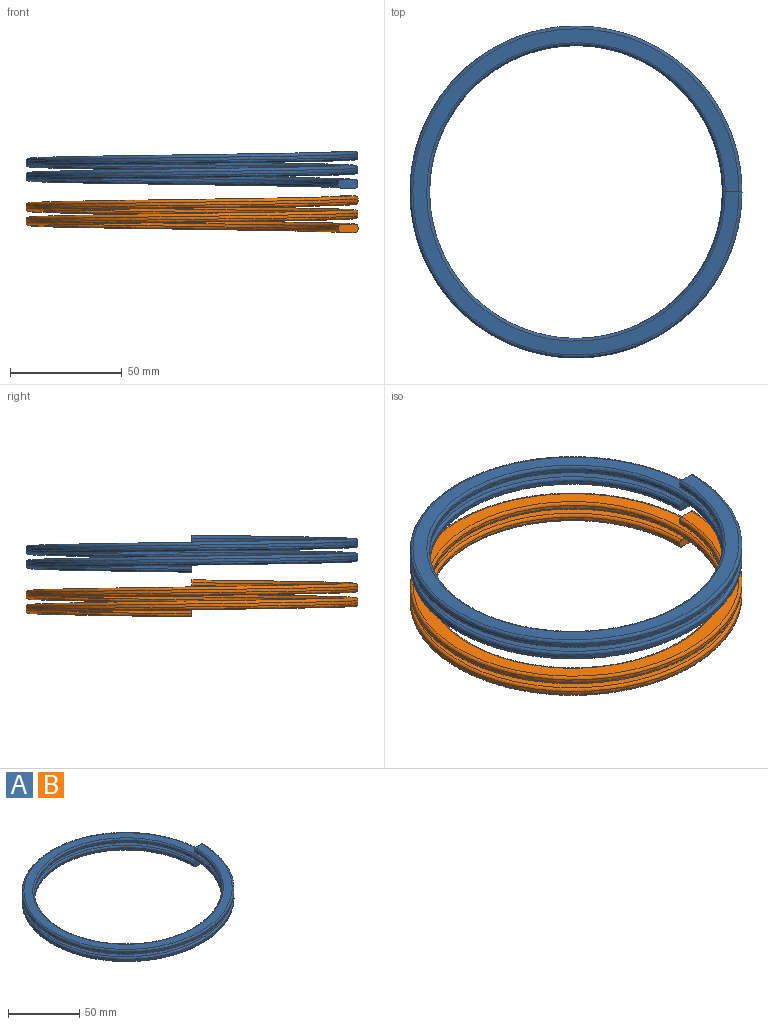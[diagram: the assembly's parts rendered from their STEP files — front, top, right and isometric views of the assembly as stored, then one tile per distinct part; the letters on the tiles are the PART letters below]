
ASSEMBLY  parts=2 mates=1
PART A: 10 faces, bbox 148.7x171.7x16.8 mm
  f0: plane 8.78x3.92mm, normal (0,-1,0), area 32.5mm2, adj f2,f3,f4,f5,f6,f7,f8,f9
  f1: plane 8.78x3.92mm, normal (0,1,0), area 32.5mm2, adj f2,f3,f4,f5,f6,f7,f8,f9
  f2: bspline ~171.65x148.65mm, area 5446.9mm2, adj f0,f1,f8,f9
  f3: cylinder r=65.59mm len=131.18mm, axis (0,0,1), area 1102mm2, adj f0,f1,f7,f8
  f4: bspline ~171.65x148.65mm, area 5446.9mm2, adj f0,f1,f6,f7
  f5: cylinder r=74.33mm len=148.65mm, axis (0,0,1), area 1248.8mm2, adj f0,f1,f6,f9
  f6: bspline ~148.71x148.68mm, area 1852.8mm2, adj f0,f1,f4,f5
  f7: bspline ~133.78x133.75mm, area 1657.8mm2, adj f0,f1,f3,f4
  f8: bspline ~133.78x133.75mm, area 1657.8mm2, adj f0,f1,f2,f3
  f9: bspline ~148.71x148.68mm, area 1852.8mm2, adj f0,f1,f2,f5
PART B: same geometry as A
PLACE A t=(-3.95,7.06,9.61)mm
PLACE B t=(-3.91,7.06,-10.39)mm
MATE slider B.f1 <-> A.f0  axis (0,1,0) through (66.05,7.06,0.22)mm
